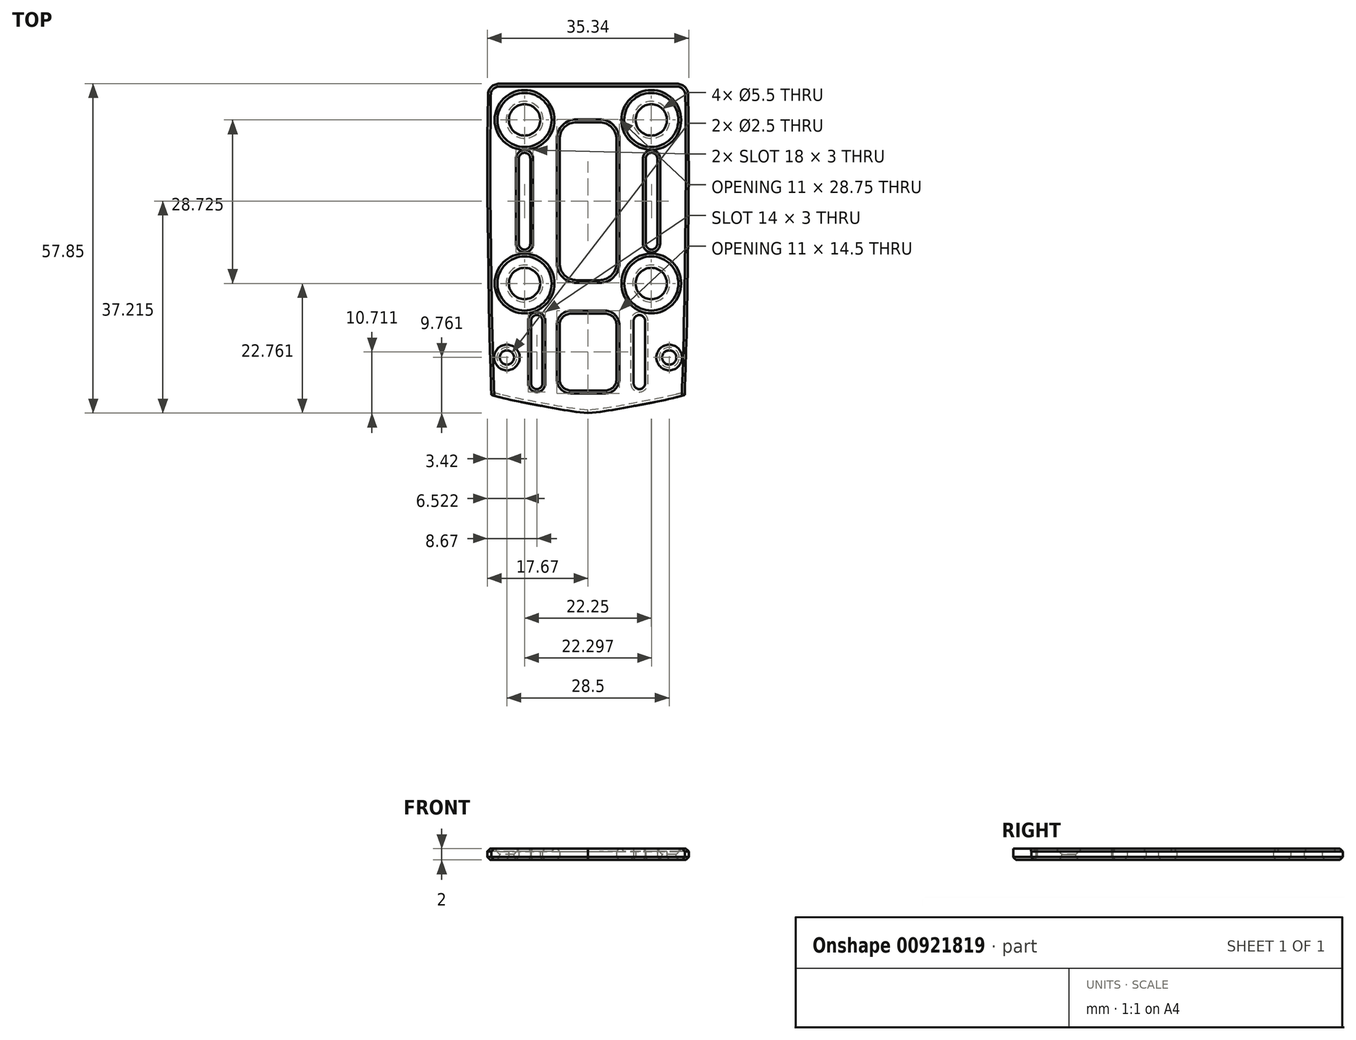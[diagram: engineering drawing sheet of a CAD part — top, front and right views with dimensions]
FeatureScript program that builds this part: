
annotation { "Feature Type Name" : "Feature", "Feature Type Description" : "" }
export const myFeature = defineFeature(function(context is Context, id is Id, definition is map)
    precondition{}
    {
        {
            var Q0;
            Q0=qCreatedBy(makeId("Top.planeOp"),FACE);
            var sketch = newSketch(context, id + "F0", { "sketchPlane" : qUnion([Q0])});
            skLineSegment(sketch, "E0", {"start": v(15.58, 12.76) * mm, "end": v(-15.58, 12.76) * mm});
            skFitSpline(sketch, "E1", {"points": [v(-17.55, 12.76) * mm, v(-17.55, -14.92) * mm, v(-16.97, -41.9) * mm], "startDerivative": vector(-1.27, -105.06) * mm, "endDerivative": vector(2.95, -84.29) * mm});
            skCircle(sketch, "E2", {"center": v(-11.15, -22.33) * mm, "radius": 2.75 * mm});
            skCircle(sketch, "E3", {"center": v(-11.15, 6.4) * mm, "radius": 2.75 * mm});
            skCircle(sketch, "E4", {"center": v(11.1, 6.4) * mm, "radius": 2.75 * mm});
            skCircle(sketch, "E5", {"center": v(11.1, -22.33) * mm, "radius": 2.75 * mm});
            skLineSegment(sketch, "E6", {"start": v(11.1, -22.33) * mm, "end": v(-19.49, -22.33) * mm, "construction": true});
            skLineSegment(sketch, "E7", {"start": v(11.1, 6.4) * mm, "end": v(-16.85, 6.4) * mm, "construction": true});
            skLineSegment(sketch, "E8.bottom", {"start": v(-2, 6) * mm, "end": v(2, 6) * mm});
            skLineSegment(sketch, "E8.top", {"start": v(-2, -21.75) * mm, "end": v(2, -21.75) * mm});
            skLineSegment(sketch, "E8.left", {"start": v(-5, 3) * mm, "end": v(-5, -18.75) * mm});
            skLineSegment(sketch, "E8.right", {"start": v(5, 3) * mm, "end": v(5, -18.75) * mm});
            skPoint(sketch, "E8.middle", {"position": v(0, -7.88) * mm});
            skPoint(sketch, "E9.visualSharp", {"position": v(-5, 6) * mm});
            skArc(sketch, "E9.filletArc", {"start": v(-2, 6) * mm, "mid": v(-4.12, 5.12) * mm, "end": v(-5, 3) * mm});
            skPoint(sketch, "E10.visualSharp", {"position": v(5, 6) * mm});
            skArc(sketch, "E10.filletArc", {"start": v(5, 3) * mm, "mid": v(4.12, 5.12) * mm, "end": v(2, 6) * mm});
            skPoint(sketch, "E11.visualSharp", {"position": v(5, -21.75) * mm});
            skArc(sketch, "E11.filletArc", {"start": v(2, -21.75) * mm, "mid": v(4.12, -20.87) * mm, "end": v(5, -18.75) * mm});
            skPoint(sketch, "E12.visualSharp", {"position": v(-5, -21.75) * mm});
            skArc(sketch, "E12.filletArc", {"start": v(-5, -18.75) * mm, "mid": v(-4.12, -20.87) * mm, "end": v(-2, -21.75) * mm});
            skFitSpline(sketch, "E13.MirrorCS", {"points": [v(17.55, 12.76) * mm, v(17.55, -14.92) * mm, v(16.97, -41.9) * mm], "startDerivative": vector(1.27, -105.06) * mm, "endDerivative": vector(-2.95, -84.29) * mm});
            skFitSpline(sketch, "E14", {"points": [v(-16.97, -41.9) * mm, v(-8.8, -43.7) * mm, v(0, -45.09) * mm], "startDerivative": vector(16.14, -4.96) * mm, "endDerivative": vector(18.25, -1.39) * mm});
            skFitSpline(sketch, "E15.MirrorCS", {"points": [v(16.97, -41.9) * mm, v(8.8, -43.7) * mm, v(0, -45.09) * mm], "startDerivative": vector(-16.14, -4.96) * mm, "endDerivative": vector(-18.25, -1.39) * mm});
            skLineSegment(sketch, "E16.left", {"start": v(-12.15, -0.37) * mm, "end": v(-12.15, -15.37) * mm});
            skLineSegment(sketch, "E16.right", {"start": v(-10.15, -0.37) * mm, "end": v(-10.15, -15.37) * mm});
            skArc(sketch, "E17", {"start": v(-12.15, -0.37) * mm, "mid": v(-11.15, 0.63) * mm, "end": v(-10.15, -0.37) * mm});
            skArc(sketch, "E18", {"start": v(-10.15, -15.37) * mm, "mid": v(-11.15, -16.37) * mm, "end": v(-12.15, -15.37) * mm});
            skLineSegment(sketch, "E19", {"start": v(-12.15, -0.37) * mm, "end": v(-10.15, -0.37) * mm, "construction": true});
            skLineSegment(sketch, "E20.MirrorCS", {"start": v(10.15, -0.37) * mm, "end": v(10.15, -15.38) * mm});
            skArc(sketch, "E21.MirrorCS", {"start": v(12.15, -0.37) * mm, "mid": v(11.15, 0.63) * mm, "end": v(10.15, -0.37) * mm});
            skLineSegment(sketch, "E22.MirrorCS", {"start": v(12.15, -0.37) * mm, "end": v(12.15, -15.37) * mm});
            skArc(sketch, "E23.MirrorCS", {"start": v(10.15, -15.38) * mm, "mid": v(11.15, -16.37) * mm, "end": v(12.15, -15.37) * mm});
            skLineSegment(sketch, "E24.bottom", {"start": v(-3, -27.63) * mm, "end": v(3, -27.63) * mm});
            skLineSegment(sketch, "E24.top", {"start": v(-3, -41.13) * mm, "end": v(3, -41.13) * mm});
            skLineSegment(sketch, "E24.left", {"start": v(-5, -29.63) * mm, "end": v(-5, -39.13) * mm});
            skLineSegment(sketch, "E24.right", {"start": v(5, -29.63) * mm, "end": v(5, -39.13) * mm});
            skPoint(sketch, "E24.middle", {"position": v(0, -34.38) * mm});
            skPoint(sketch, "E25.visualSharp", {"position": v(-5, -27.63) * mm});
            skArc(sketch, "E25.filletArc", {"start": v(-3, -27.63) * mm, "mid": v(-4.41, -28.21) * mm, "end": v(-5, -29.63) * mm});
            skPoint(sketch, "E26.visualSharp", {"position": v(5, -27.63) * mm});
            skArc(sketch, "E26.filletArc", {"start": v(5, -29.63) * mm, "mid": v(4.41, -28.21) * mm, "end": v(3, -27.63) * mm});
            skPoint(sketch, "E27.visualSharp", {"position": v(5, -41.13) * mm});
            skArc(sketch, "E27.filletArc", {"start": v(3, -41.13) * mm, "mid": v(4.41, -40.54) * mm, "end": v(5, -39.13) * mm});
            skPoint(sketch, "E28.visualSharp", {"position": v(-5, -41.13) * mm});
            skArc(sketch, "E28.filletArc", {"start": v(-5, -39.13) * mm, "mid": v(-4.41, -40.54) * mm, "end": v(-3, -41.13) * mm});
            skLineSegment(sketch, "E29", {"start": v(-10, -28.88) * mm, "end": v(-10, -39.88) * mm});
            skLineSegment(sketch, "E30", {"start": v(-8, -28.88) * mm, "end": v(-8, -39.88) * mm});
            skLineSegment(sketch, "E31", {"start": v(-10, -28.88) * mm, "end": v(-8, -28.88) * mm, "construction": true});
            skArc(sketch, "E32", {"start": v(-10, -28.88) * mm, "mid": v(-9, -27.88) * mm, "end": v(-8, -28.88) * mm});
            skArc(sketch, "E33", {"start": v(-10, -39.88) * mm, "mid": v(-9, -40.88) * mm, "end": v(-8, -39.88) * mm});
            skLineSegment(sketch, "E34.MirrorCS", {"start": v(8, -28.88) * mm, "end": v(8, -39.88) * mm});
            skArc(sketch, "E35.MirrorCS", {"start": v(10, -28.88) * mm, "mid": v(9, -27.88) * mm, "end": v(8, -28.88) * mm});
            skLineSegment(sketch, "E36.MirrorCS", {"start": v(10, -28.88) * mm, "end": v(10, -39.88) * mm});
            skArc(sketch, "E37.MirrorCS", {"start": v(10, -39.88) * mm, "mid": v(9, -40.88) * mm, "end": v(8, -39.88) * mm});
            skLineSegment(sketch, "E38", {"start": v(11.1, 6.4) * mm, "end": v(11.1, -23.42) * mm, "construction": true});
            skLineSegment(sketch, "E39", {"start": v(-5, -7.87) * mm, "end": v(-10.15, -7.87) * mm, "construction": true});
            skLineSegment(sketch, "E40", {"start": v(-5, -34.38) * mm, "end": v(-8, -34.38) * mm, "construction": true});
            skArc(sketch, "E41.filletArc", {"start": v(-15.58, 12.76) * mm, "mid": v(-16.98, 12.18) * mm, "end": v(-17.58, 10.78) * mm});
            skArc(sketch, "E42.filletArc", {"start": v(17.58, 10.78) * mm, "mid": v(16.98, 12.18) * mm, "end": v(15.58, 12.76) * mm});
            skArc(sketch, "E43.filletArc", {"start": v(15.52, -42.31) * mm, "mid": v(16.58, -41.63) * mm, "end": v(17.02, -40.45) * mm});
            skArc(sketch, "E44.filletArc", {"start": v(-17.02, -40.45) * mm, "mid": v(-16.58, -41.63) * mm, "end": v(-15.52, -42.31) * mm});
            skCircle(sketch, "E45.0", {"center": v(-11.15, -22.33) * mm, "radius": 4.75 * mm});
            skCircle(sketch, "E46.0", {"center": v(11.1, -22.33) * mm, "radius": 4.75 * mm});
            skCircle(sketch, "E47.0", {"center": v(-11.15, 6.4) * mm, "radius": 4.75 * mm});
            skCircle(sketch, "E48.0", {"center": v(11.1, 6.4) * mm, "radius": 4.75 * mm});
            skLineSegment(sketch, "E49", {"start": v(-14.25, -35.33) * mm, "end": v(14.25, -35.33) * mm, "construction": true});
            skLineSegment(sketch, "E50", {"start": v(0, -32.27) * mm, "end": v(0, -35.33) * mm, "construction": true});
            skLineSegment(sketch, "E51", {"start": v(-11.15, -22.33) * mm, "end": v(-11.15, -15.37) * mm, "construction": true});
            skSolve(sketch);
        }
        {
            var Q0;
            Q0 = qSketchRegion(id + "F0", true);
            extrude(context, id + "F1", {"entities" : qUnion([Q0]), "depth" : 2 * mm, "offsetDistance" : 25 * mm});
        }
        {
            var Q0;
            Q0=makeQuery(id+"F0.imprint","IMPRINT",FACE,{"disambiguationData":[TD([[makeQuery(id+"F0.imprint","IMPRINT",EDGE,{"derivedFrom":sQuery(id+"F0.wireOp",EDGE,"E3")}),-1.0]])]});
            var Q1;
            Q1=makeQuery(id+"F0.imprint","IMPRINT",FACE,{"disambiguationData":[TD([[makeQuery(id+"F0.imprint","IMPRINT",EDGE,{"derivedFrom":sQuery(id+"F0.wireOp",EDGE,"E4")}),-1.0]])]});
            var Q2;
            Q2=makeQuery(id+"F0.imprint","IMPRINT",FACE,{"disambiguationData":[TD([[makeQuery(id+"F0.imprint","IMPRINT",EDGE,{"derivedFrom":sQuery(id+"F0.wireOp",EDGE,"E2")}),-1.0]])]});
            var Q3;
            Q3=makeQuery(id+"F0.imprint","IMPRINT",FACE,{"disambiguationData":[TD([[makeQuery(id+"F0.imprint","IMPRINT",EDGE,{"derivedFrom":sQuery(id+"F0.wireOp",EDGE,"E5")}),-1.0]])]});
            extrude(context, id + "F2", {"entities" : qUnion([Q0, Q1, Q2, Q3]), "operationType" : NewBodyOperationType.ADD, "depth" : 1.5 * mm, "offsetDistance" : 25 * mm});
        }
        {
            var Q0;
            Q0=makeQuery(id+"F1.opExtrude","CAP_FACE",FACE,{"disambiguationData":[OSD([sQuery(id+"F0.wireOp",EDGE,"E0"),sQuery(id+"F0.wireOp",EDGE,"E1"),sQuery(id+"F0.wireOp",EDGE,"E8.bottom"),sQuery(id+"F0.wireOp",EDGE,"E8.top"),sQuery(id+"F0.wireOp",EDGE,"E8.left"),sQuery(id+"F0.wireOp",EDGE,"E8.right"),sQuery(id+"F0.wireOp",EDGE,"E9.filletArc"),sQuery(id+"F0.wireOp",EDGE,"E10.filletArc"),sQuery(id+"F0.wireOp",EDGE,"E11.filletArc"),sQuery(id+"F0.wireOp",EDGE,"E12.filletArc"),sQuery(id+"F0.wireOp",EDGE,"E13.MirrorCS"),sQuery(id+"F0.wireOp",EDGE,"E14"),sQuery(id+"F0.wireOp",EDGE,"E15.MirrorCS"),sQuery(id+"F0.wireOp",EDGE,"E16.left"),sQuery(id+"F0.wireOp",EDGE,"E16.right"),sQuery(id+"F0.wireOp",EDGE,"E17"),sQuery(id+"F0.wireOp",EDGE,"E18"),sQuery(id+"F0.wireOp",EDGE,"E20.MirrorCS"),sQuery(id+"F0.wireOp",EDGE,"E21.MirrorCS"),sQuery(id+"F0.wireOp",EDGE,"E22.MirrorCS"),sQuery(id+"F0.wireOp",EDGE,"E23.MirrorCS"),sQuery(id+"F0.wireOp",EDGE,"E24.bottom"),sQuery(id+"F0.wireOp",EDGE,"E24.top"),sQuery(id+"F0.wireOp",EDGE,"E24.left"),sQuery(id+"F0.wireOp",EDGE,"E24.right"),sQuery(id+"F0.wireOp",EDGE,"E25.filletArc"),sQuery(id+"F0.wireOp",EDGE,"E26.filletArc"),sQuery(id+"F0.wireOp",EDGE,"E27.filletArc"),sQuery(id+"F0.wireOp",EDGE,"E28.filletArc"),sQuery(id+"F0.wireOp",EDGE,"E29"),sQuery(id+"F0.wireOp",EDGE,"E30"),sQuery(id+"F0.wireOp",EDGE,"E32"),sQuery(id+"F0.wireOp",EDGE,"E33"),sQuery(id+"F0.wireOp",EDGE,"E34.MirrorCS"),sQuery(id+"F0.wireOp",EDGE,"E35.MirrorCS"),sQuery(id+"F0.wireOp",EDGE,"E36.MirrorCS"),sQuery(id+"F0.wireOp",EDGE,"E37.MirrorCS"),sQuery(id+"F0.wireOp",EDGE,"E41.filletArc"),sQuery(id+"F0.wireOp",EDGE,"E42.filletArc"),sQuery(id+"F0.wireOp",EDGE,"E43.filletArc"),sQuery(id+"F0.wireOp",EDGE,"E44.filletArc"),sQuery(id+"F0.wireOp",EDGE,"E45.0"),sQuery(id+"F0.wireOp",EDGE,"E46.0"),sQuery(id+"F0.wireOp",EDGE,"E47.0"),sQuery(id+"F0.wireOp",EDGE,"E48.0")])],"isStart":false});
            var sketch = newSketch(context, id + "F3", { "sketchPlane" : qUnion([Q0])});
            skPoint(sketch, "E52.0", {"position": v(-14.25, -35.33) * mm});
            skPoint(sketch, "E53.0", {"position": v(14.25, -35.33) * mm});
            skSolve(sketch);
        }
        {
            var Q0;
            Q0=sQuery(id+"F3.wireOp",VERTEX,"E52.0");
            var Q1;
            Q1=sQuery(id+"F3.wireOp",VERTEX,"E53.0");
            var Q2;
            Q2=makeQuery(id+"F1.opExtrude","SWEPT_BODY",BODY,{"disambiguationData":[OSD([sQuery(id+"F0.wireOp",EDGE,"E0"),sQuery(id+"F0.wireOp",EDGE,"E1"),sQuery(id+"F0.wireOp",EDGE,"E8.bottom"),sQuery(id+"F0.wireOp",EDGE,"E8.top"),sQuery(id+"F0.wireOp",EDGE,"E8.left"),sQuery(id+"F0.wireOp",EDGE,"E8.right"),sQuery(id+"F0.wireOp",EDGE,"E9.filletArc"),sQuery(id+"F0.wireOp",EDGE,"E10.filletArc"),sQuery(id+"F0.wireOp",EDGE,"E11.filletArc"),sQuery(id+"F0.wireOp",EDGE,"E12.filletArc"),sQuery(id+"F0.wireOp",EDGE,"E13.MirrorCS"),sQuery(id+"F0.wireOp",EDGE,"E14"),sQuery(id+"F0.wireOp",EDGE,"E15.MirrorCS"),sQuery(id+"F0.wireOp",EDGE,"E16.left"),sQuery(id+"F0.wireOp",EDGE,"E16.right"),sQuery(id+"F0.wireOp",EDGE,"E17"),sQuery(id+"F0.wireOp",EDGE,"E18"),sQuery(id+"F0.wireOp",EDGE,"E20.MirrorCS"),sQuery(id+"F0.wireOp",EDGE,"E21.MirrorCS"),sQuery(id+"F0.wireOp",EDGE,"E22.MirrorCS"),sQuery(id+"F0.wireOp",EDGE,"E23.MirrorCS"),sQuery(id+"F0.wireOp",EDGE,"E24.bottom"),sQuery(id+"F0.wireOp",EDGE,"E24.top"),sQuery(id+"F0.wireOp",EDGE,"E24.left"),sQuery(id+"F0.wireOp",EDGE,"E24.right"),sQuery(id+"F0.wireOp",EDGE,"E25.filletArc"),sQuery(id+"F0.wireOp",EDGE,"E26.filletArc"),sQuery(id+"F0.wireOp",EDGE,"E27.filletArc"),sQuery(id+"F0.wireOp",EDGE,"E28.filletArc"),sQuery(id+"F0.wireOp",EDGE,"E29"),sQuery(id+"F0.wireOp",EDGE,"E30"),sQuery(id+"F0.wireOp",EDGE,"E32"),sQuery(id+"F0.wireOp",EDGE,"E33"),sQuery(id+"F0.wireOp",EDGE,"E34.MirrorCS"),sQuery(id+"F0.wireOp",EDGE,"E35.MirrorCS"),sQuery(id+"F0.wireOp",EDGE,"E36.MirrorCS"),sQuery(id+"F0.wireOp",EDGE,"E37.MirrorCS"),sQuery(id+"F0.wireOp",EDGE,"E41.filletArc"),sQuery(id+"F0.wireOp",EDGE,"E42.filletArc"),sQuery(id+"F0.wireOp",EDGE,"E43.filletArc"),sQuery(id+"F0.wireOp",EDGE,"E44.filletArc"),sQuery(id+"F0.wireOp",EDGE,"E45.0"),sQuery(id+"F0.wireOp",EDGE,"E46.0"),sQuery(id+"F0.wireOp",EDGE,"E47.0"),sQuery(id+"F0.wireOp",EDGE,"E48.0")])]});
            hole(context, id + "F4", {"style" : HoleStyle.C_SINK, "endStyle" : HoleEndStyle.THROUGH, "holeDiameter" : 2.5 * mm, "cSinkDiameter" : 4.5 * mm, "cSinkAngle" : 90 * degree, "majorDiameter" : 5 * mm, "isTappedThrough" : true, "tappedDepth" : 12 * mm, "tapClearance" : 3, "locations" : qUnion([Q0, Q1]), "scope" : qUnion([Q2])});
        }
        {
            var Q0;
            {var subQ0=sQuery(id+"F0.wireOp",EDGE,"E46.0");var subQ1=sQuery(id+"F0.wireOp",EDGE,"E48.0");var subQ2=sQuery(id+"F0.wireOp",EDGE,"E47.0");var subQ3=sQuery(id+"F0.wireOp",EDGE,"E45.0");Q0=makeQuery(id+"F2.boolean.opBoolean","MERGE",FACE,{"derivedFrom":[makeQuery(id+"F1.opExtrude","CAP_FACE",FACE,{"disambiguationData":[OSD([sQuery(id+"F0.wireOp",EDGE,"E0"),sQuery(id+"F0.wireOp",EDGE,"E1"),sQuery(id+"F0.wireOp",EDGE,"E8.bottom"),sQuery(id+"F0.wireOp",EDGE,"E8.top"),sQuery(id+"F0.wireOp",EDGE,"E8.left"),sQuery(id+"F0.wireOp",EDGE,"E8.right"),sQuery(id+"F0.wireOp",EDGE,"E9.filletArc"),sQuery(id+"F0.wireOp",EDGE,"E10.filletArc"),sQuery(id+"F0.wireOp",EDGE,"E11.filletArc"),sQuery(id+"F0.wireOp",EDGE,"E12.filletArc"),sQuery(id+"F0.wireOp",EDGE,"E13.MirrorCS"),sQuery(id+"F0.wireOp",EDGE,"E14"),sQuery(id+"F0.wireOp",EDGE,"E15.MirrorCS"),sQuery(id+"F0.wireOp",EDGE,"E16.left"),sQuery(id+"F0.wireOp",EDGE,"E16.right"),sQuery(id+"F0.wireOp",EDGE,"E17"),sQuery(id+"F0.wireOp",EDGE,"E18"),sQuery(id+"F0.wireOp",EDGE,"E20.MirrorCS"),sQuery(id+"F0.wireOp",EDGE,"E21.MirrorCS"),sQuery(id+"F0.wireOp",EDGE,"E22.MirrorCS"),sQuery(id+"F0.wireOp",EDGE,"E23.MirrorCS"),sQuery(id+"F0.wireOp",EDGE,"E24.bottom"),sQuery(id+"F0.wireOp",EDGE,"E24.top"),sQuery(id+"F0.wireOp",EDGE,"E24.left"),sQuery(id+"F0.wireOp",EDGE,"E24.right"),sQuery(id+"F0.wireOp",EDGE,"E25.filletArc"),sQuery(id+"F0.wireOp",EDGE,"E26.filletArc"),sQuery(id+"F0.wireOp",EDGE,"E27.filletArc"),sQuery(id+"F0.wireOp",EDGE,"E28.filletArc"),sQuery(id+"F0.wireOp",EDGE,"E29"),sQuery(id+"F0.wireOp",EDGE,"E30"),sQuery(id+"F0.wireOp",EDGE,"E32"),sQuery(id+"F0.wireOp",EDGE,"E33"),sQuery(id+"F0.wireOp",EDGE,"E34.MirrorCS"),sQuery(id+"F0.wireOp",EDGE,"E35.MirrorCS"),sQuery(id+"F0.wireOp",EDGE,"E36.MirrorCS"),sQuery(id+"F0.wireOp",EDGE,"E37.MirrorCS"),sQuery(id+"F0.wireOp",EDGE,"E41.filletArc"),sQuery(id+"F0.wireOp",EDGE,"E42.filletArc"),sQuery(id+"F0.wireOp",EDGE,"E43.filletArc"),sQuery(id+"F0.wireOp",EDGE,"E44.filletArc"),subQ3,subQ0,subQ2,subQ1])],"isStart":true}),makeQuery(id+"F2.opExtrude","CAP_FACE",FACE,{"disambiguationData":[OSD([sQuery(id+"F0.wireOp",EDGE,"E2"),subQ3])],"isStart":true}),makeQuery(id+"F2.opExtrude","CAP_FACE",FACE,{"disambiguationData":[OSD([sQuery(id+"F0.wireOp",EDGE,"E3"),subQ2])],"isStart":true}),makeQuery(id+"F2.opExtrude","CAP_FACE",FACE,{"disambiguationData":[OSD([sQuery(id+"F0.wireOp",EDGE,"E4"),subQ1])],"isStart":true}),makeQuery(id+"F2.opExtrude","CAP_FACE",FACE,{"disambiguationData":[OSD([sQuery(id+"F0.wireOp",EDGE,"E5"),subQ0])],"isStart":true})]});}
            var Q1;
            Q1=makeQuery(id+"F1.opExtrude","CAP_EDGE",EDGE,{"disambiguationData":[OSD([sQuery(id+"F0.wireOp",EDGE,"E1")])],"isStart":false});
            var Q2;
            Q2=makeQuery(id+"F1.opExtrude","CAP_EDGE",EDGE,{"disambiguationData":[OSD([sQuery(id+"F0.wireOp",EDGE,"E29")])],"isStart":false});
            var Q3;
            Q3=makeQuery(id+"F1.opExtrude","CAP_EDGE",EDGE,{"disambiguationData":[OSD([sQuery(id+"F0.wireOp",EDGE,"E24.left")])],"isStart":false});
            var Q4;
            Q4=makeQuery(id+"F1.opExtrude","CAP_EDGE",EDGE,{"disambiguationData":[OSD([sQuery(id+"F0.wireOp",EDGE,"E8.left")])],"isStart":false});
            var Q5;
            Q5=makeQuery(id+"F1.opExtrude","CAP_EDGE",EDGE,{"disambiguationData":[OSD([sQuery(id+"F0.wireOp",EDGE,"E16.right")])],"isStart":false});
            var Q6;
            Q6=makeQuery(id+"F1.opExtrude","CAP_EDGE",EDGE,{"disambiguationData":[OSD([sQuery(id+"F0.wireOp",EDGE,"E45.0")])],"isStart":false});
            var Q7;
            Q7=makeQuery(id+"F1.opExtrude","CAP_EDGE",EDGE,{"disambiguationData":[OSD([sQuery(id+"F0.wireOp",EDGE,"E46.0")])],"isStart":false});
            var Q8;
            Q8=makeQuery(id+"F1.opExtrude","CAP_EDGE",EDGE,{"disambiguationData":[OSD([sQuery(id+"F0.wireOp",EDGE,"E48.0")])],"isStart":false});
            var Q9;
            Q9=makeQuery(id+"F1.opExtrude","CAP_EDGE",EDGE,{"disambiguationData":[OSD([sQuery(id+"F0.wireOp",EDGE,"E20.MirrorCS")])],"isStart":false});
            var Q10;
            Q10=makeQuery(id+"F1.opExtrude","CAP_EDGE",EDGE,{"disambiguationData":[OSD([sQuery(id+"F0.wireOp",EDGE,"E47.0")])],"isStart":false});
            chamfer(context, id + "F5", {"entities" : qUnion([Q0, Q1, Q2, Q3, Q4, Q5, Q6, Q7, Q8, Q9, Q10]), "width" : 0.5 * mm, "tangentPropagation" : true});
        }
    });
